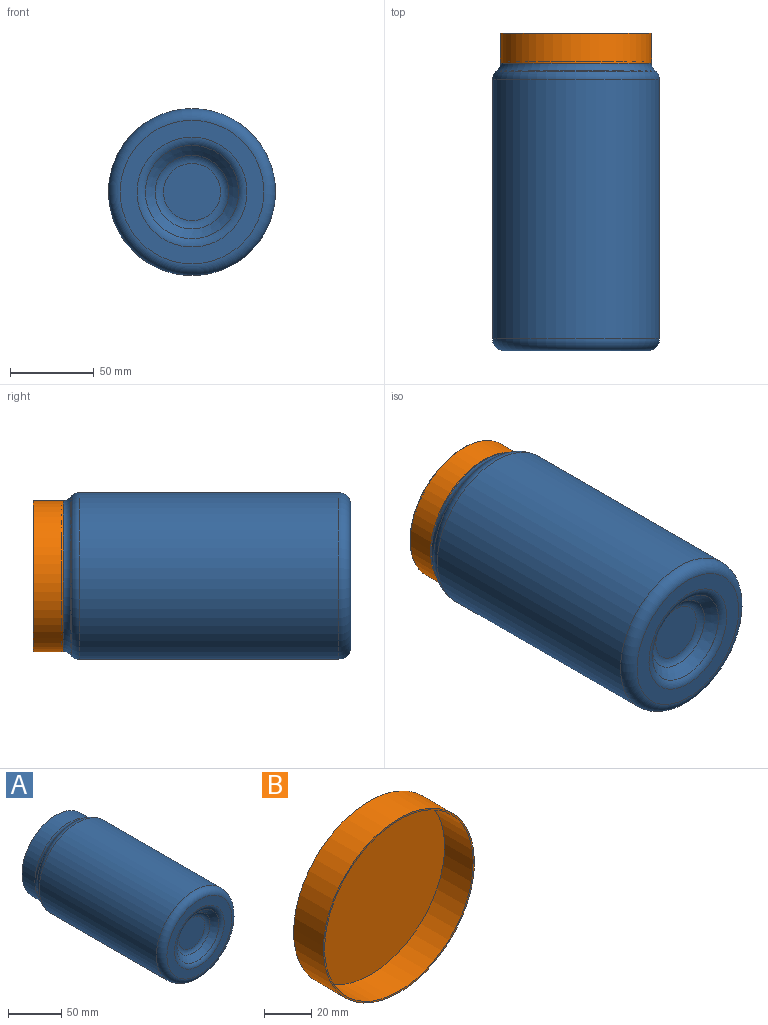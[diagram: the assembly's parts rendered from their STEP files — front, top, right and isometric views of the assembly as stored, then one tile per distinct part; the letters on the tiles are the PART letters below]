
ASSEMBLY  parts=2 mates=1
PART A: 23 faces, bbox 112.6x190x112.6 mm
  f0: cylinder r=50mm len=155.1mm, axis (0,1,0), area 48726.3mm2, adj f1,f22
  f1: torus R=43mm, axis (0,1,0), area 3278.6mm2, adj f0,f2
  f2: plane 86x86mm, normal (0,-1,0), area 2408.4mm2, adj f1,f3
  f3: torus R=32.9mm, axis (0,1,0), area 1046.3mm2, adj f2,f4
  f4: cone r=27.95mm half-angle=45deg, axis (0,-1,0), area 1310.5mm2, adj f3,f5
  f5: torus R=17.1mm, axis (0,1,0), area 680.9mm2, adj f4,f6
  f6: plane 34.2x34.2mm, normal (0,-1,0), area 918.7mm2, adj f5
  f7: plane 34.2x34.2mm, normal (0,1,0), area 918.7mm2, adj f8
  f8: torus R=17.1mm, axis (0,1,0), area 764.5mm2, adj f7,f9
  f9: cone r=28.48mm half-angle=45deg, axis (0,-1,0), area 1338.3mm2, adj f8,f10
  f10: torus R=32.9mm, axis (0,1,0), area 942.8mm2, adj f9,f11
  f11: plane 86x86mm, normal (0,1,0), area 2408.4mm2, adj f10,f12
  f12: torus R=43mm, axis (0,1,0), area 2897.9mm2, adj f11,f13
  f13: cylinder r=49.25mm len=155.1mm, axis (0,1,0), area 47995.4mm2, adj f12,f14
  f14: torus R=43mm, axis (0,1,0), area 1499.8mm2, adj f13,f15
  f15: cone r=46.52mm half-angle=45deg, axis (0,-1,0), area 375.4mm2, adj f14,f16
  f16: torus R=52mm, axis (0,1,0), area 1721.9mm2, adj f15,f17
  f17: cylinder r=44.25mm len=88.5mm, axis (0,1,0), area 4754.5mm2, adj f16,f18
  f18: plane 90x90mm, normal (0,1,0), area 210.3mm2, adj f17,f19
  f19: cylinder r=45mm len=90mm, axis (0,1,0), area 4835.1mm2, adj f18,f20
  f20: torus R=52mm, axis (0,1,0), area 1578.6mm2, adj f19,f21
  f21: cone r=47.05mm half-angle=45deg, axis (0,-1,0), area 379.7mm2, adj f20,f22
  f22: torus R=43mm, axis (0,1,0), area 1703.1mm2, adj f0,f21
PART B: 5 faces, bbox 90.5x17.9x90.5 mm
  f0: plane 89x89mm, normal (0,-1,0), area 6221.1mm2, adj f4
  f1: plane 90.5x90.5mm, normal (0,1,0), area 6432.6mm2, adj f2
  f2: cylinder r=45.25mm len=90.5mm, axis (0,-1,0), area 5075.2mm2, adj f1,f3
  f3: plane 90.5x90.5mm, normal (0,-1,0), area 211.5mm2, adj f2,f4
  f4: cylinder r=44.5mm len=89mm, axis (0,-1,0), area 4781.3mm2, adj f0,f3
PLACE A t=(0,-95,0)mm
PLACE B t=(0,-17.85,0)mm
MATE fastened B.f2 <-> A.f0  axis (0,-1,0) through (0,0,0)mm
